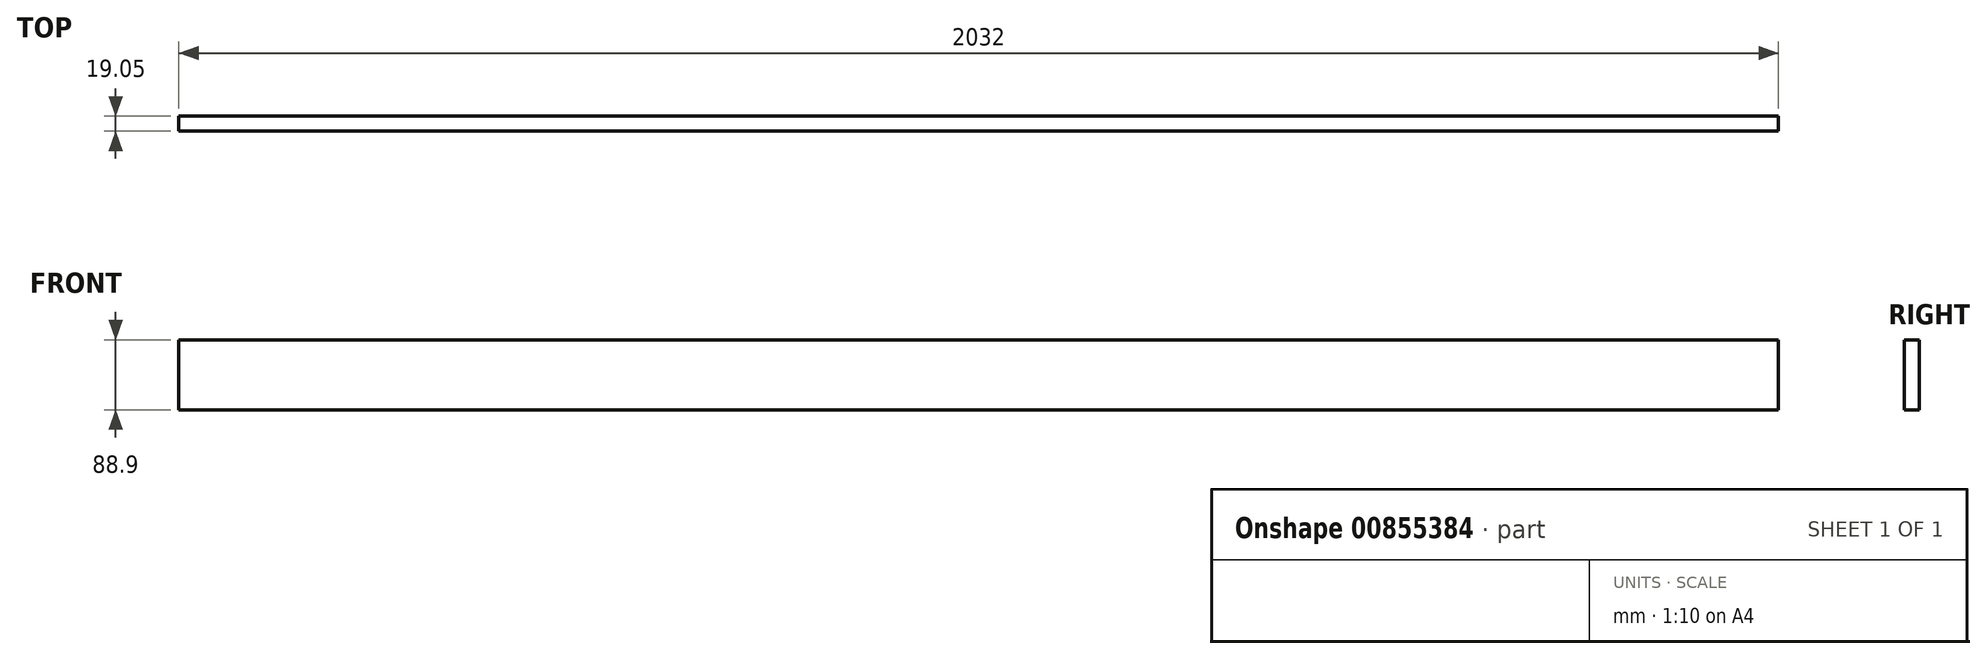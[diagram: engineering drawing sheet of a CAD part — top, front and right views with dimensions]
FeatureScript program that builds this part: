
annotation { "Feature Type Name" : "Feature", "Feature Type Description" : "" }
export const myFeature = defineFeature(function(context is Context, id is Id, definition is map)
    precondition{}
    {
        {
            var Q0;
            Q0=qCreatedBy(makeId("Right.planeOp"),FACE);
            var sketch = newSketch(context, id + "F0", { "sketchPlane" : qUnion([Q0])});
            skLineSegment(sketch, "E0.bottom", {"start": v(0, 0) * mm, "end": v(19.05, 0) * mm});
            skLineSegment(sketch, "E0.top", {"start": v(0, 88.9) * mm, "end": v(19.05, 88.9) * mm});
            skLineSegment(sketch, "E0.left", {"start": v(0, 0) * mm, "end": v(0, 88.9) * mm});
            skLineSegment(sketch, "E0.right", {"start": v(19.05, 0) * mm, "end": v(19.05, 88.9) * mm});
            skSolve(sketch);
        }
        {
            var Q0;
            Q0 = qSketchRegion(id + "F0", true);
            extrude(context, id + "F1", {"entities" : qUnion([Q0]), "depth" : 2032 * mm, "offsetDistance" : 25.4 * mm});
        }
    });
